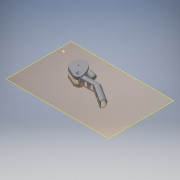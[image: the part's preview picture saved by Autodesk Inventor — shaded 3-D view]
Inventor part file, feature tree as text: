
AUTODESK INVENTOR PART (.ipt)
format: ipt  version: 2016 (Build 200138000, 138)  size: 2,321,920 bytes
history: native  units: mm
features: sketch x54, plane x35, extrude x18, fillet x15, sweep x5, chamfer x2, projected_geometry x2, loft x1, mirror x1, split x1
ambient origin geometry x8: Origin, YZ Plane, XZ Plane, XY Plane, X Axis, Y Axis, Z Axis, Center Point
bodies: Solid1 (feature_tree), Solid5 (feature_tree), Solid6 (feature_tree)
feature tree (134):
  sketch  "Sketch1"  dims[d1=8.0mm d2=7.0mm]
  plane  "Work Plane4"
  sketch  "Sketch2"  dims[d3=7.0mm d4=8.0mm d8=20.0mm d9=-3.490659mm d11=8.0mm d12=8.0mm d14=2.0mm d15=10.0mm d17=-1.745329mm d18=1.0mm d19=11.75mm]
  sketch  "Sketch3"  dims[d20=20.0mm d21=9.5mm]
  sketch  "Sketch4"  dims[d22=8.0mm d23=0.0mm d25=9.0mm]
  sketch  "Sketch5"  dims[d27=8.5mm d28=3.0mm]
  sketch  "Sketch6"  dims[d29=-1.745329mm d30=-3.490659mm d31=1.0mm d32=2.0mm d33=8.6mm]
  plane  "Work Plane5"
  sketch  "Sketch7"  dims[d34=8.5mm d35=7.0mm]
  plane  "Work Plane7"
  sketch  "Sketch8"  dims[d36=7.0mm d37=5.0mm d38=3.0mm d39=17.0mm]
  plane  "Work Plane8"
  sketch  "Sketch9"  dims[d40=8.0mm d41=17.0mm]
  plane  "Work Plane10"
  sketch  "Sketch10"  dims[d42=7.7mm d43=17.0mm]
  plane  "Work Plane11"
  plane  "Work Plane12"
  sketch  "Sketch11"  dims[d44=6.8mm]
  sketch  "Sketch12"  dims[d45=17.0mm]
  sketch  "Sketch13"  dims[d46=5.0mm]
  plane  "Work Plane13"
  plane  "Work Plane14"
  plane  "Work Plane15"
  plane  "Work Plane16"
  sketch  "Sketch14"  dims[d47=2.0mm]
  sketch  "Sketch15"  dims[d48=17.0mm]
  plane  "Work Plane20"
  sketch  "Sketch16"  dims[d49=2.0mm]
  sketch  "Sketch17"  dims[d50=2.0mm d51=0.0mm d52=90.0deg]
  sketch  "Sketch18"  dims[d53=0.0mm d54=90.0deg d55=0.0mm d56=90.0deg]
  sketch  "Sketch19"  dims[d57=0.0mm d58=90.0deg d59=0.0mm d60=90.0deg]
  plane  "Work Plane21"
  loft  "Loft1"
  extrude  "Extrusion1"  Depth=10.0mm
  fillet  "Fillet1"  [1 undecoded]
  fillet  "Fillet2"  Radius=8.0mm
  fillet  "Fillet3"  Radius=2.0mm
  fillet  "Fillet4"  Radius=10.0mm
  fillet  "Fillet5"  Radius=1.0mm
  fillet  "Fillet6"  Radius=11.75mm
  plane  "Work Plane23"
  plane  "Work Plane25"
  sketch  "Sketch22"  dims[d77=0.0mm d78=90.0deg d79=0.0mm d80=90.0deg d81=0.0mm d82=90.0deg]
  extrude  "Extrusion2"  Depth=9.5mm
  plane  "Work Plane26"
  sketch  "Sketch24"  dims[d89=135.0deg d90=2.0mm]
  sketch  "Sketch25"  dims[d91=45.0deg d92=15.0mm d93=0.0mm]
  extrude  "Extrusion3"  Depth=9.0mm
  extrude  "Extrusion4"  Depth=3.0mm
  sketch  "Sketch27"  dims[d97=2.0mm d98=2.0mm]
  extrude  "Extrusion5"  Depth=8.6mm
  sketch  "Sketch29"  dims[d102=12.217305mm d103=20.0mm d110=3.0mm]
  extrude  "Extrusion6"  Depth=7.0mm
  extrude  "Extrusion7"  Depth=5.0mm
  mirror  "Mirror1"
  fillet  "Fillet10"  Radius=17.0mm
  sketch  "Sketch31"  dims[d113=6.0mm d114=20.0mm d115=0.0mm]
  plane  "Work Plane27"
  extrude  "Extrusion9"  Depth=17.0mm
  extrude  "Extrusion10"  Depth=17.0mm
  chamfer  "Chamfer4"  Angle=90.0deg  [1 undecoded]
  extrude  "Extrusion11"  TaperAngle=0.0deg  [1 undecoded]
  extrude  "Extrusion12"  TaperAngle=0.0deg  [1 undecoded]
  extrude  "Extrusion13"  TaperAngle=0.0deg  [1 undecoded]
  chamfer  "Chamfer5"  Angle=90.0deg  [1 undecoded]
  fillet  "Fillet19"  [1 undecoded]
  fillet  "Fillet20"  [1 undecoded]
  plane  "Work Plane37"
  plane  "Work Plane48"
  sketch  "Sketch63"  dims[d126=12.0mm]
  sketch  "Sketch47"  dims[d125=4.0mm]
  fillet  "Fillet21"  [1 undecoded]
  plane  "Work Plane39"
  plane  "Work Plane40"
  split  "Split2"
  plane  "Work Plane47"
  plane  "Work Plane49"
  sweep  "Sweep11"
  plane  "Work Plane50"
  sweep  "Sweep12"
  fillet  "Fillet22"  [1 undecoded]
  sweep  "Sweep13"
  fillet  "Fillet23"  Radius=6.0mm
  fillet  "Fillet24"  Radius=6.0mm
  fillet  "Fillet25"  Radius=2.0mm
  sketch  "Sketch94"  dims[d143=1.2mm]
  sketch  "Sketch95"  dims[d144=12.0mm d145=0.0mm]
  extrude  "Extrusion39"  Depth=2.0mm
  extrude  "Extrusion40"  Depth=15.0mm TaperAngle=0.0deg
  extrude  "Extrusion41"  Depth=2.0mm
  fillet  "Fillet26"  Radius=2.0mm
  sweep  "Sweep6"
  extrude  "Extrusion32"  Depth=22.0mm TaperAngle=90.0deg
  extrude  "Extrusion33"  Depth=3.0mm
  sketch  "Sketch71"  dims[d130=10.75mm]
  sketch  "Sketch72"  dims[d131=9.0mm]
  sweep  "Sweep8"
  sketch  "Sketch74"  dims[d132=9.0mm]
  plane  "Work Plane43"
  extrude  "Extrusion36"  Depth=20.0mm TaperAngle=0.0deg
  plane  "Work Plane1"
  plane  "Work Plane2"
  plane  "Work Plane3"
  plane  "Work Plane6"
  plane  "Work Plane9"
  plane  "Work Plane17"
  plane  "Work Plane18"
  plane  "Work Plane19"
  sketch  "Sketch20"  dims[d61=0.0mm d62=90.0deg d63=0.0mm d64=90.0deg d65=0.0mm d66=90.0deg d67=0.0mm d68=90.0deg d69=0.0mm d70=90.0deg d71=0.0mm d72=90.0deg]
  sketch  "Sketch21"  dims[d73=0.0mm d74=90.0deg d75=0.0mm d76=90.0deg]
  plane  "Work Plane22"
  plane  "Work Plane24"
  sketch  "Sketch23"  dims[d83=0.0mm d84=90.0deg d85=0.3mm d86=6.0mm d87=6.0mm d88=2.0mm]
  sketch  "Sketch26"  dims[d94=2.0mm d95=2.0mm d96=2.0mm]
  sketch  "Sketch28"  dims[d99=2.0mm d100=90.0deg d101=22.0mm]
  sketch  "Sketch30"  dims[d111=6.0mm d112=8.0mm]
  sketch  "Sketch32"  dims[d116=12.0mm]
  sketch  "Sketch33"  dims[d117=20.0mm]
  sketch  "Sketch34"  dims[d118=10.0mm]
  sketch  "Sketch35"  dims[d123=2.0mm]
  sketch  "Sketch36"  dims[d124=4.0mm]
  sketch  "Sketch68"  dims[d127=6.0mm]
  sketch  "Sketch70"  dims[d128=6.0mm d129=0.0mm]
  projected_geometry  "Projected Loop1"
  sketch  "Sketch77"  dims[d133=60.0mm d134=0.0mm]
  projected_geometry  "Projected Loop2"
  sketch  "Sketch81"  dims[d135=30.0mm]
  sketch  "Sketch83"  dims[d136=2.0mm]
  sketch  "Sketch84"  dims[d137=12.0mm]
  sketch  "Sketch86"  dims[d138=6.0mm d139=0.0mm]
  sketch  "Sketch87"  dims[d140=1.2mm]
  sketch  "Sketch89"  dims[d141=8.0mm]
  sketch  "Sketch92"  dims[d142=8.0mm]
  sketch  "Sketch96"  dims[d146=20.0mm d147=0.0mm d154=1.0mm d167=4.2mm d168=0.0mm d172=4.5mm d173=2.7mm d174=0.0mm d175=2.0mm d176=2.0mm d177=45.0deg d178=2.8mm d179=0.0mm d180=14.0mm d181=4.2mm d182=0.0mm d183=2.8mm d184=0.0mm d185=2.0mm d186=2.0mm d187=45.0deg d262=3.85mm d263=1.0mm d264=0.25mm d265=-31.0mm d303=2.5mm d304=5.5mm d305=2.25mm d313=0.25mm d315=-2.1mm d316=52.0mm d317=10.2mm d318=7.5mm d321=2.0mm d322=0.5mm d323=0.5mm d324=2.0mm d325=1.0mm d326=1.5mm d327=1.0mm d328=1.5mm d329=4.0mm d330=0.0mm d335=2.0mm d337=2.0mm d338=0.0mm d339=57.6mm d340=3.0mm d341=3.0mm d342=2.0mm d345=26.598818mm d346=2.939134mm d347=3.263766mm d348=35.5mm d349=6.9mm d350=16.0mm d351=36.8mm d352=5.394mm d358=0.0mm d359=0.0mm d362=0.0mm d363=0.0mm d371=2.0mm d374=1.5mm d375=0.0mm d386=9.0mm d389=1.0mm d392=0.0mm d393=0.0mm d394=5.524714mm d395=2.5mm d396=6.0mm d397=6.5mm d400=0.0mm d401=0.0mm d402=2.0mm d403=8.0mm d405=7.0mm d406=1.0mm d415=0.0mm d416=0.0mm d418=1.0mm d419=0.5mm d420=0.5mm d421=3.0mm d423=19.0mm d424=24.0mm d425=7.417649mm d426=13.439035mm d427=9.0mm d428=3.5mm d429=5.0mm d430=12.0mm d431=3.5mm d432=5.0mm d435=1.0mm d436=0.0mm d437=2.0mm d438=3.5mm d439=5.0mm d440=1.0mm d441=0.0mm d448=7.0mm d449=0.0mm d450=0.5mm d451=5.323254mm d452=7.0mm]
note: 10 required parameter values undecoded (feature->parameter linkage not recoverable at this tier; creation-order binding heuristic only, values carry confidence <= 0.55)
